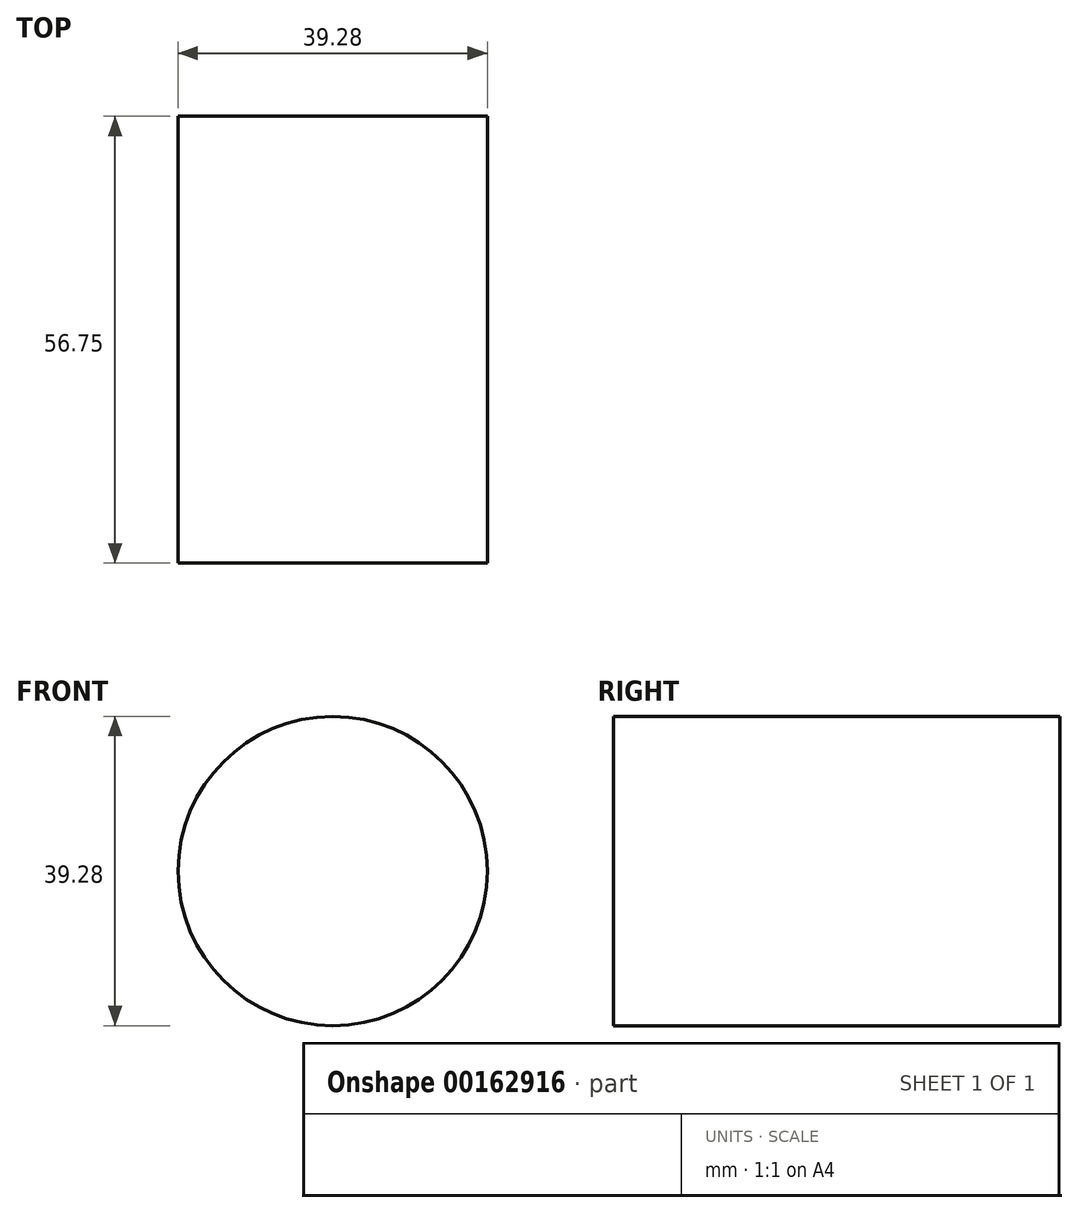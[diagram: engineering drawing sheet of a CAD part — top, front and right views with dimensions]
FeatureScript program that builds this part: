
annotation { "Feature Type Name" : "Feature", "Feature Type Description" : "" }
export const myFeature = defineFeature(function(context is Context, id is Id, definition is map)
    precondition{}
    {
        {
            var Q0;
            Q0=qCreatedBy(makeId("Front.planeOp"),FACE);
            var sketch = newSketch(context, id + "F0", { "sketchPlane" : qUnion([Q0])});
            skCircle(sketch, "E0", {"center": v(0, 0) * mm, "radius": 19.64 * mm});
            skSolve(sketch);
        }
        {
            var Q0;
            Q0 = qSketchRegion(id + "F0", true);
            extrude(context, id + "F1", {"entities" : qUnion([Q0]), "depth" : 56.75 * mm});
        }
    });
